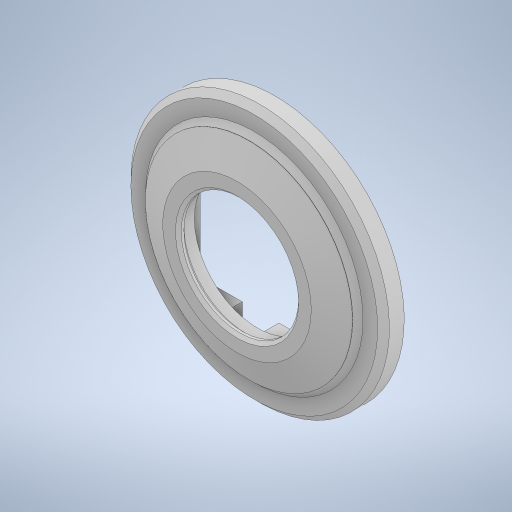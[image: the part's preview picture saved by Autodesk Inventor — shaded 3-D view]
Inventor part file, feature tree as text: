
AUTODESK INVENTOR PART (.ipt)
format: ipt  version: 2023 (Build 270158000, 158)  size: 353,280 bytes
history: native  units: mm
features: extrude x8, sketch x8, chamfer x5, projected_geometry x1
ambient origin geometry x8: Origin, YZ Plane, XZ Plane, XY Plane, X Axis, Y Axis, Z Axis, Center Point
bodies: Solid1 (feature_tree)
feature tree (22):
  extrude  "Extrusion1"  Depth=52.95mm
  extrude  "Extrusion2"  Depth=10.35mm TaperAngle=0.0deg
  extrude  "Extrusion3"  Depth=32.0mm
  extrude  "Extrusion4"  Depth=34.5mm
  extrude  "Extrusion5"  Depth=40.8mm
  chamfer  "Chamfer1"  [1 undecoded]
  extrude  "Extrusion6"  Depth=10.0mm TaperAngle=45.0deg
  chamfer  "Chamfer4"  Distance=5.0mm
  extrude  "Extrusion7"  Depth=10.0mm
  extrude  "Extrusion8"  Depth=10.0mm
  chamfer  "Chamfer5"  Distance=4.5mm
  chamfer  "Chamfer6"  Distance=21.5mm
  chamfer  "Chamfer7"  Distance=7.0mm
  sketch  "Sketch1"  dims[d0=66.5mm d1=52.95mm]
  sketch  "Sketch2"  dims[d2=2.0mm d3=10.35mm d4=0.0mm]
  sketch  "Sketch3"  dims[d5=0.5mm d6=0.0mm d7=32.0mm]
  sketch  "Sketch4"  dims[d8=2.5mm d9=0.0mm d10=34.5mm]
  sketch  "Sketch5"  dims[d11=3.1mm d12=0.0mm d13=40.8mm]
  sketch  "Sketch6"  dims[d14=35.7mm]
  projected_geometry  "Projected Loop1"
  sketch  "Sketch7"  dims[d15=17.85mm]
  sketch  "Sketch8"  dims[d16=20.4mm d17=0.0mm d18=0.0mm d19=0.8mm d20=2.0mm d21=45.0deg d25=5.0mm d26=0.0mm d30=1.0mm d31=2.0mm d32=2.792527mm d36=10.0mm d38=4.5mm d39=0.0mm d40=21.5mm d41=7.0mm d42=4.7mm d43=0.0mm d44=8.0mm d45=2.0mm d46=3.839724mm d47=1.6mm d48=2.0mm d49=3.839724mm d50=1.4mm d51=2.0mm d52=3.839724mm]
note: 1 required parameter value undecoded (feature->parameter linkage not recoverable at this tier; creation-order binding heuristic only, values carry confidence <= 0.55)
